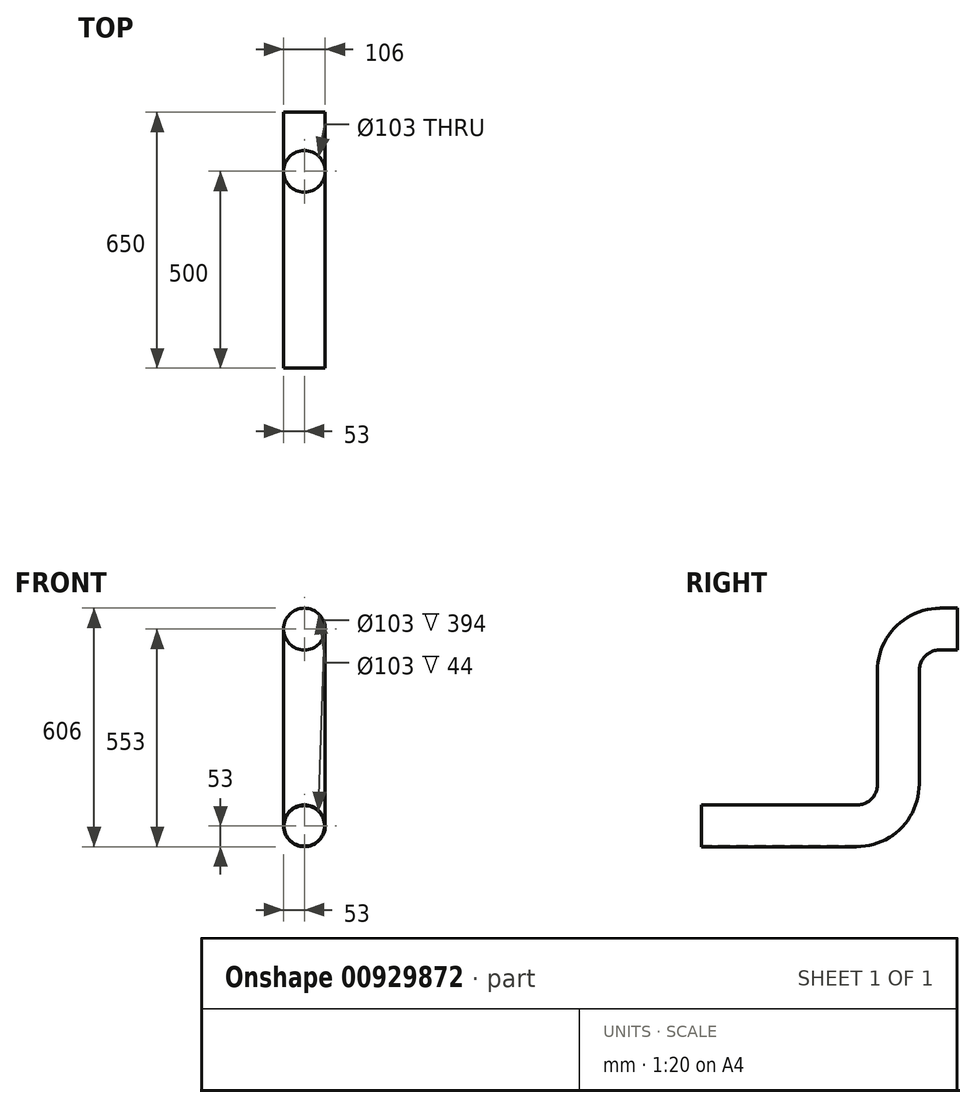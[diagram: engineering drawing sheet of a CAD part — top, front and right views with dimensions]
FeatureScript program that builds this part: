
annotation { "Feature Type Name" : "Feature", "Feature Type Description" : "" }
export const myFeature = defineFeature(function(context is Context, id is Id, definition is map)
    precondition{}
    {
        {
            var Q0;
            Q0=qCreatedBy(makeId("Front.planeOp"),FACE);
            var sketch = newSketch(context, id + "F0", { "sketchPlane" : qUnion([Q0])});
            skCircle(sketch, "E0", {"center": v(0, 0) * mm, "radius": 53 * mm});
            skCircle(sketch, "E1", {"center": v(0, 0) * mm, "radius": 51.5 * mm});
            skSolve(sketch);
        }
        {
            var Q0;
            Q0=qCreatedBy(makeId("Right.planeOp"),FACE);
            var sketch = newSketch(context, id + "F1", { "sketchPlane" : qUnion([Q0])});
            skLineSegment(sketch, "E2", {"start": v(0, 0) * mm, "end": v(-44, 0) * mm});
            skLineSegment(sketch, "E3", {"start": v(-150, -106) * mm, "end": v(-150, -394) * mm});
            skLineSegment(sketch, "E4", {"start": v(-256, -500) * mm, "end": v(-650, -500) * mm});
            skPoint(sketch, "E5.visualSharp", {"position": v(-150, 0) * mm});
            skArc(sketch, "E5.filletArc", {"start": v(-44, 0) * mm, "mid": v(-118.95, -31.05) * mm, "end": v(-150, -106) * mm});
            skPoint(sketch, "E6.visualSharp", {"position": v(-150, -500) * mm});
            skArc(sketch, "E6.filletArc", {"start": v(-256, -500) * mm, "mid": v(-181.05, -468.95) * mm, "end": v(-150, -394) * mm});
            skSolve(sketch);
        }
        {
            var Q0;
            Q0=makeQuery(id+"F0.imprint","IMPRINT",FACE,{"disambiguationData":[TD([[makeQuery(id+"F0.imprint","IMPRINT",EDGE,{"derivedFrom":sQuery(id+"F0.wireOp",EDGE,"E0")}),1.0]])]});
            var Q1;
            Q1=sQuery(id+"F1.wireOp",EDGE,"E2");
            var Q2;
            Q2=sQuery(id+"F1.wireOp",EDGE,"E5.filletArc");
            var Q3;
            Q3=sQuery(id+"F1.wireOp",EDGE,"E3");
            var Q4;
            Q4=sQuery(id+"F1.wireOp",EDGE,"E6.filletArc");
            var Q5;
            Q5=sQuery(id+"F1.wireOp",EDGE,"E4");
            sweep(context, id + "F2", {"profiles" : qUnion([Q0]), "path" : qUnion([Q1, Q2, Q3, Q4, Q5])});
        }
    });
